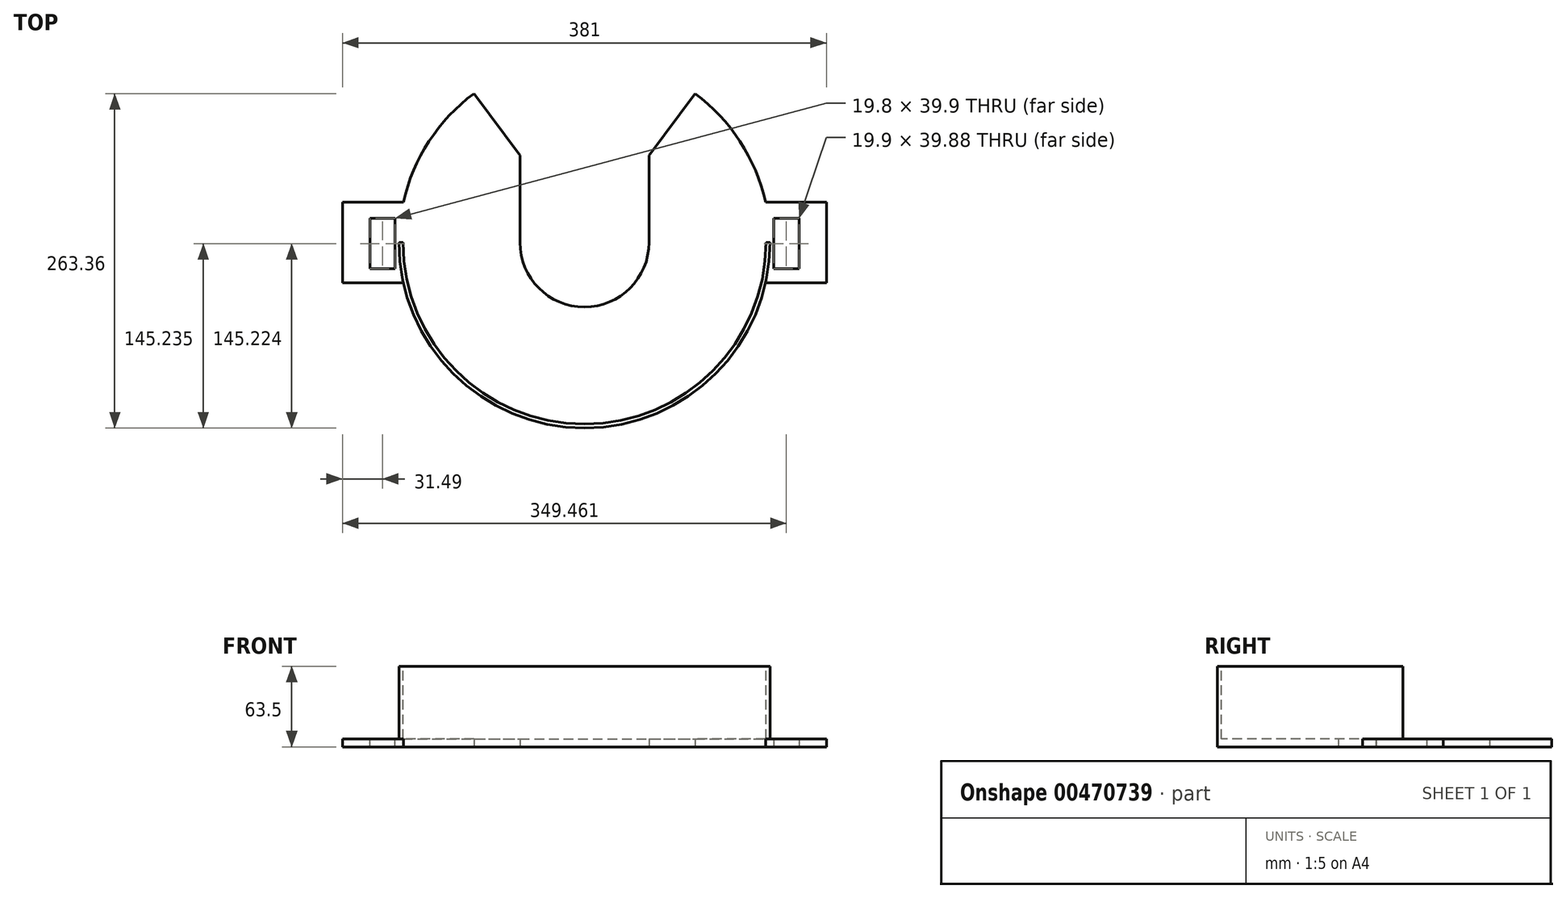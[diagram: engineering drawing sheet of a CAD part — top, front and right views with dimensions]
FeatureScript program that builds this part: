
annotation { "Feature Type Name" : "Feature", "Feature Type Description" : "" }
export const myFeature = defineFeature(function(context is Context, id is Id, definition is map)
    precondition{}
    {
        {
            var Q0;
            Q0=qCreatedBy(makeId("Top.planeOp"),FACE);
            var sketch = newSketch(context, id + "F0", { "sketchPlane" : qUnion([Q0])});
            skCircle(sketch, "E0", {"center": v(0, 0) * mm, "radius": 146.05 * mm});
            skSolve(sketch);
        }
        {
            var Q0;
            Q0=makeQuery(id+"F0.imprint","IMPRINT",FACE,{"disambiguationData":[TD([[makeQuery(id+"F0.imprint","IMPRINT",EDGE,{"derivedFrom":sQuery(id+"F0.wireOp",EDGE,"E0")}),1.0]])]});
            extrude(context, id + "F1", {"entities" : qUnion([Q0]), "depth" : 63.5 * mm});
        }
        {
            var Q0;
            Q0=makeQuery(id+"F1.opExtrude","CAP_FACE",FACE,{"disambiguationData":[OSD([sQuery(id+"F0.wireOp",EDGE,"E0")])],"isStart":false});
            var sketch = newSketch(context, id + "F2", { "sketchPlane" : qUnion([Q0])});
            skCircle(sketch, "E1", {"center": v(0, 0) * mm, "radius": 142.88 * mm});
            skSolve(sketch);
        }
        {
            var Q0;
            Q0=makeQuery(id+"F2.imprint","IMPRINT",FACE,{"disambiguationData":[TD([[makeQuery(id+"F2.imprint","IMPRINT",EDGE,{"derivedFrom":sQuery(id+"F2.wireOp",EDGE,"E1")}),1.0]])]});
            extrude(context, id + "F3", {"entities" : qUnion([Q0]), "operationType" : NewBodyOperationType.REMOVE, "depth" : -57.15 * mm});
        }
        {
            var Q0;
            Q0=makeQuery(id+"F2.imprint","IMPRINT",FACE,{"disambiguationData":[TD([[makeQuery(id+"F2.imprint","IMPRINT",EDGE,{"derivedFrom":sQuery(id+"F2.wireOp",EDGE,"E1")}),1.0]])]});
            var sketch = newSketch(context, id + "F4", { "sketchPlane" : qUnion([Q0])});
            skLineSegment(sketch, "E2.bottom", {"start": v(186.45, 0) * mm, "end": v(-190.86, 0) * mm});
            skLineSegment(sketch, "E2.top", {"start": v(186.45, 147.84) * mm, "end": v(-190.86, 147.84) * mm});
            skLineSegment(sketch, "E2.left", {"start": v(186.45, 0) * mm, "end": v(186.45, 147.84) * mm});
            skLineSegment(sketch, "E2.right", {"start": v(-190.86, 0) * mm, "end": v(-190.86, 147.84) * mm});
            skSolve(sketch);
        }
        {
            var Q0;
            Q0=makeQuery(id+"F4.imprint","IMPRINT",FACE,{"disambiguationData":[TD([[makeQuery(id+"F4.imprint","IMPRINT",EDGE,{"derivedFrom":sQuery(id+"F4.wireOp",EDGE,"E2.top")}),1.0]])]});
            extrude(context, id + "F5", {"entities" : qUnion([Q0]), "operationType" : NewBodyOperationType.REMOVE, "oppositeDirection" : true, "depth" : 57.15 * mm});
        }
        {
            var Q0;
            Q0=makeQuery(id+"F2.imprint","IMPRINT",FACE,{"disambiguationData":[TD([[makeQuery(id+"F2.imprint","IMPRINT",EDGE,{"derivedFrom":sQuery(id+"F2.wireOp",EDGE,"E1")}),1.0]])]});
            var sketch = newSketch(context, id + "F6", { "sketchPlane" : qUnion([Q0])});
            skArc(sketch, "E3", {"start": v(94.56, 127.51) * mm, "mid": v(0, 159.46) * mm, "end": v(-94.56, 127.51) * mm});
            skLineSegment(sketch, "E4", {"start": v(0, 0) * mm, "end": v(94.56, 127.51) * mm});
            skLineSegment(sketch, "E5", {"start": v(-94.56, 127.51) * mm, "end": v(0, 0) * mm});
            skSolve(sketch);
        }
        {
            var Q0;
            Q0=qSketchRegion(id+"F6",true);
            extrude(context, id + "F7", {"entities" : qUnion([Q0]), "operationType" : NewBodyOperationType.REMOVE, "endBound" : BoundingType.THROUGH_ALL, "oppositeDirection" : true, "depth" : 25.4 * mm});
        }
        {
            var Q0;
            Q0=qCreatedBy(makeId("Top.planeOp"),FACE);
            var sketch = newSketch(context, id + "F8", { "sketchPlane" : qUnion([Q0])});
            skLineSegment(sketch, "E6.bottom", {"start": v(-190.5, -31.68) * mm, "end": v(190.5, -31.68) * mm});
            skLineSegment(sketch, "E6.top", {"start": v(-190.5, 31.82) * mm, "end": v(190.5, 31.82) * mm});
            skLineSegment(sketch, "E6.left", {"start": v(-190.5, -31.68) * mm, "end": v(-190.5, 31.82) * mm});
            skLineSegment(sketch, "E6.right", {"start": v(190.5, -31.68) * mm, "end": v(190.5, 31.82) * mm});
            skSolve(sketch);
        }
        {
            var Q0;
            Q0=makeQuery(id+"F8.imprint","IMPRINT",FACE,{"disambiguationData":[TD([[makeQuery(id+"F8.imprint","IMPRINT",EDGE,{"derivedFrom":sQuery(id+"F8.wireOp",EDGE,"E6.bottom")}),1.0]])]});
            extrude(context, id + "F9", {"entities" : qUnion([Q0]), "operationType" : NewBodyOperationType.ADD, "depth" : 6.35 * mm});
        }
        {
            var Q0;
            {var subQ0=sQuery(id+"F2.wireOp",EDGE,"E1");Q0=makeQuery(id+"F9.boolean.opBoolean","MERGE",FACE,{"derivedFrom":[makeQuery(id+"F5.boolean.opBoolean","MERGE",FACE,{"derivedFrom":[makeQuery(id+"F3.boolean.opBoolean","COPY",FACE,{"derivedFrom":makeQuery(id+"F3.opExtrude","CAP_FACE",FACE,{"disambiguationData":[OSD([subQ0])],"isStart":false})}),makeQuery(id+"F5.opExtrude","CAP_FACE",FACE,{"disambiguationData":[OSD([subQ0,sQuery(id+"F4.wireOp",EDGE,"E2.bottom"),sQuery(id+"F4.wireOp",EDGE,"E2.top"),sQuery(id+"F4.wireOp",EDGE,"E2.left"),sQuery(id+"F4.wireOp",EDGE,"E2.right")])],"isStart":false})]}),makeQuery(id+"F9.opExtrude","CAP_FACE",FACE,{"disambiguationData":[OSD([sQuery(id+"F8.wireOp",EDGE,"E6.bottom"),sQuery(id+"F8.wireOp",EDGE,"E6.top"),sQuery(id+"F8.wireOp",EDGE,"E6.left"),sQuery(id+"F8.wireOp",EDGE,"E6.right")])],"isStart":false})]});}
            var sketch = newSketch(context, id + "F10", { "sketchPlane" : qUnion([Q0])});
            skLineSegment(sketch, "E7.bottom", {"start": v(-168.91, 19.12) * mm, "end": v(-149.11, 19.12) * mm});
            skLineSegment(sketch, "E7.top", {"start": v(-168.91, -20.78) * mm, "end": v(-149.11, -20.78) * mm});
            skLineSegment(sketch, "E7.left", {"start": v(-168.91, 19.12) * mm, "end": v(-168.91, -20.78) * mm});
            skLineSegment(sketch, "E7.right", {"start": v(-149.11, 19.12) * mm, "end": v(-149.11, -20.78) * mm});
            skSolve(sketch);
        }
        {
            var Q0;
            Q0 = qSketchRegion(id + "F10", true);
            extrude(context, id + "F11", {"entities" : qUnion([Q0]), "operationType" : NewBodyOperationType.REMOVE, "oppositeDirection" : true, "depth" : 6.35 * mm});
        }
        {
            var Q0;
            Q0=qCreatedBy(makeId("Top.planeOp"),FACE);
            var sketch = newSketch(context, id + "F12", { "sketchPlane" : qUnion([Q0])});
            skLineSegment(sketch, "E8.bottom", {"start": v(168.91, 19.12) * mm, "end": v(149.01, 19.12) * mm});
            skLineSegment(sketch, "E8.top", {"start": v(168.91, -20.75) * mm, "end": v(149.01, -20.75) * mm});
            skLineSegment(sketch, "E8.left", {"start": v(168.91, 19.12) * mm, "end": v(168.91, -20.75) * mm});
            skLineSegment(sketch, "E8.right", {"start": v(149.01, 19.12) * mm, "end": v(149.01, -20.75) * mm});
            skSolve(sketch);
        }
        {
            var Q0;
            Q0 = qSketchRegion(id + "F12", true);
            extrude(context, id + "F13", {"entities" : qUnion([Q0]), "operationType" : NewBodyOperationType.REMOVE, "depth" : 6.35 * mm});
        }
        {
            var Q0;
            Q0=qCreatedBy(makeId("Top.planeOp"),FACE);
            var sketch = newSketch(context, id + "F14", { "sketchPlane" : qUnion([Q0])});
            skCircle(sketch, "E9", {"center": v(0, 0) * mm, "radius": 50.8 * mm});
            skSolve(sketch);
        }
        {
            var Q0;
            Q0 = qSketchRegion(id + "F14", true);
            extrude(context, id + "F15", {"entities" : qUnion([Q0]), "operationType" : NewBodyOperationType.REMOVE, "depth" : 6.35 * mm});
        }
        {
            var Q0;
            Q0=qCreatedBy(makeId("Top.planeOp"),FACE);
            var sketch = newSketch(context, id + "F16", { "sketchPlane" : qUnion([Q0])});
            skLineSegment(sketch, "E10.bottom", {"start": v(50.8, 0) * mm, "end": v(-50.8, 0) * mm});
            skLineSegment(sketch, "E10.top", {"start": v(50.8, 81.28) * mm, "end": v(-50.8, 81.28) * mm});
            skLineSegment(sketch, "E10.left", {"start": v(50.8, 0) * mm, "end": v(50.8, 81.28) * mm});
            skLineSegment(sketch, "E10.right", {"start": v(-50.8, 0) * mm, "end": v(-50.8, 81.28) * mm});
            skPoint(sketch, "E10.middle", {"position": v(0, 40.64) * mm});
            skSolve(sketch);
        }
        {
            var Q0;
            Q0 = qSketchRegion(id + "F16", true);
            extrude(context, id + "F17", {"entities" : qUnion([Q0]), "operationType" : NewBodyOperationType.REMOVE, "endBound" : BoundingType.THROUGH_ALL, "depth" : 25.4 * mm});
        }
    });
